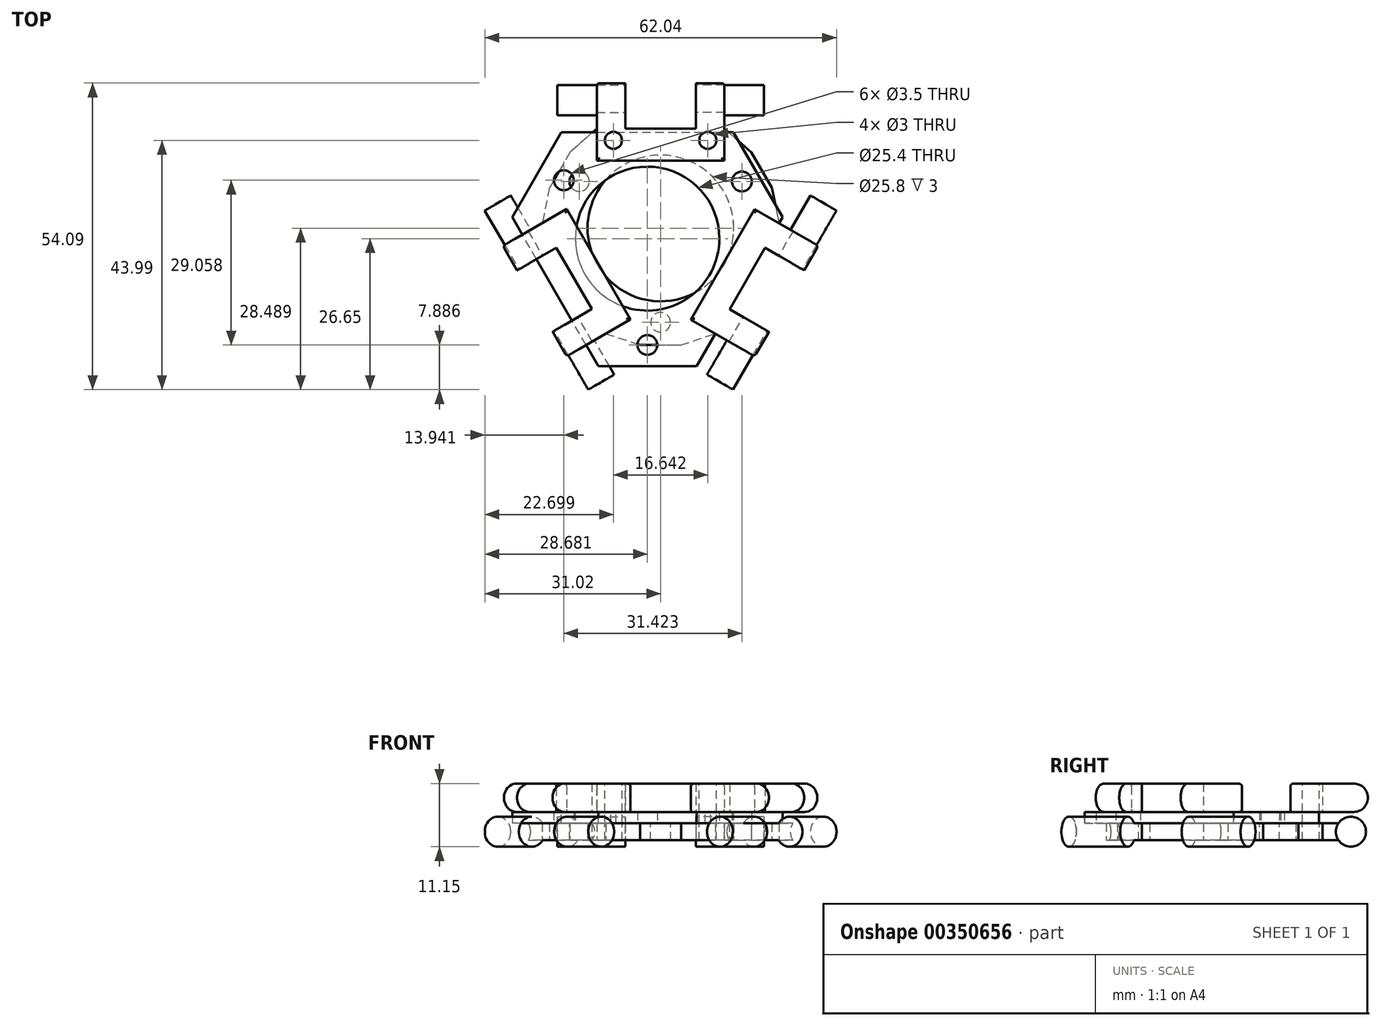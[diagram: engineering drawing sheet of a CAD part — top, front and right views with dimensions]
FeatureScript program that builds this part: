
annotation { "Feature Type Name" : "Feature", "Feature Type Description" : "" }
export const myFeature = defineFeature(function(context is Context, id is Id, definition is map)
    precondition{}
    {
        {
            var Q0;
            Q0=qCreatedBy(makeId("Top.planeOp"),FACE);
            var sketch = newSketch(context, id + "F0", { "sketchPlane" : qUnion([Q0])});
            skLineSegment(sketch, "E0", {"start": v(11.25, 26.96) * mm, "end": v(11.25, 31.96) * mm});
            skLineSegment(sketch, "E1", {"start": v(11.25, 31.96) * mm, "end": v(6.25, 31.96) * mm});
            skLineSegment(sketch, "E2", {"start": v(6.25, 31.96) * mm, "end": v(6.25, 26.96) * mm});
            skLineSegment(sketch, "E3", {"start": v(6.25, 26.96) * mm, "end": v(-6.25, 26.96) * mm});
            skLineSegment(sketch, "E4", {"start": v(-6.25, 26.96) * mm, "end": v(-6.25, 31.96) * mm});
            skLineSegment(sketch, "E5", {"start": v(-6.25, 31.96) * mm, "end": v(-11.25, 31.96) * mm});
            skLineSegment(sketch, "E6", {"start": v(-11.25, 31.96) * mm, "end": v(-11.25, 26.96) * mm});
            skLineSegment(sketch, "E7", {"start": v(11.25, 26.96) * mm, "end": v(16, 22.72) * mm});
            skLineSegment(sketch, "E8", {"start": v(-11.25, 26.96) * mm, "end": v(-16, 22.72) * mm});
            skLineSegment(sketch, "E9", {"start": v(16, 22.72) * mm, "end": v(19.6, 16.48) * mm});
            skLineSegment(sketch, "E10", {"start": v(-16, 22.72) * mm, "end": v(-19.6, 16.48) * mm});
            skLineSegment(sketch, "E11", {"start": v(-19.6, 16.48) * mm, "end": v(-20.9, 10.24) * mm});
            skLineSegment(sketch, "E12", {"start": v(19.6, 16.48) * mm, "end": v(20.9, 10.24) * mm});
            skLineSegment(sketch, "E13", {"start": v(-20.9, 10.24) * mm, "end": v(-25.23, 7.74) * mm});
            skLineSegment(sketch, "E14", {"start": v(-25.23, 7.74) * mm, "end": v(-22.73, 3.41) * mm});
            skLineSegment(sketch, "E15", {"start": v(-22.73, 3.41) * mm, "end": v(-18.4, 5.91) * mm});
            skLineSegment(sketch, "E16", {"start": v(-18.4, 5.91) * mm, "end": v(-12.15, -4.91) * mm});
            skLineSegment(sketch, "E17", {"start": v(-12.15, -4.91) * mm, "end": v(-16.48, -7.41) * mm});
            skLineSegment(sketch, "E18", {"start": v(-16.48, -7.41) * mm, "end": v(-13.98, -11.74) * mm});
            skLineSegment(sketch, "E19", {"start": v(-13.98, -11.74) * mm, "end": v(-9.65, -9.24) * mm});
            skLineSegment(sketch, "E20", {"start": v(20.9, 10.24) * mm, "end": v(25.23, 7.74) * mm});
            skLineSegment(sketch, "E21", {"start": v(25.23, 7.74) * mm, "end": v(22.73, 3.41) * mm});
            skLineSegment(sketch, "E22", {"start": v(22.73, 3.41) * mm, "end": v(18.4, 5.91) * mm});
            skLineSegment(sketch, "E23", {"start": v(18.4, 5.91) * mm, "end": v(12.15, -4.91) * mm});
            skLineSegment(sketch, "E24", {"start": v(12.15, -4.91) * mm, "end": v(16.48, -7.41) * mm});
            skLineSegment(sketch, "E25", {"start": v(16.48, -7.41) * mm, "end": v(13.98, -11.74) * mm});
            skLineSegment(sketch, "E26", {"start": v(13.98, -11.74) * mm, "end": v(9.65, -9.24) * mm});
            skLineSegment(sketch, "E27", {"start": v(-9.65, -9.24) * mm, "end": v(-3.6, -11.24) * mm});
            skLineSegment(sketch, "E28", {"start": v(-3.6, -11.24) * mm, "end": v(3.6, -11.24) * mm});
            skLineSegment(sketch, "E29", {"start": v(3.6, -11.24) * mm, "end": v(9.65, -9.24) * mm});
            skPoint(sketch, "E30.first.point", {"position": v(0, 26.96) * mm});
            skPoint(sketch, "E30.second.point", {"position": v(15.27, 0.5) * mm});
            skPoint(sketch, "E30.third.point", {"position": v(-15.27, 0.5) * mm});
            skCircle(sketch, "E31", {"center": v(0, 9.36) * mm, "radius": 12.9 * mm});
            skLineSegment(sketch, "E32", {"start": v(-17.8, 19.6) * mm, "end": v(15.27, 0.5) * mm, "construction": true});
            skLineSegment(sketch, "E33", {"start": v(17.8, 19.6) * mm, "end": v(-15.27, 0.5) * mm, "construction": true});
            skLineSegment(sketch, "E34", {"start": v(0, -11.24) * mm, "end": v(0, 26.96) * mm, "construction": true});
            skSolve(sketch);
        }
        {
            var Q0;
            Q0=qSketchRegion(id+"F0",true);
            extrude(context, id + "F1", {"entities" : qUnion([Q0]), "depth" : 3 * mm});
        }
        {
            var Q0;
            Q0=makeQuery(id+"F1.opExtrude","CAP_FACE",FACE,{"disambiguationData":[OSD([sQuery(id+"F0.wireOp",EDGE,"E0"),sQuery(id+"F0.wireOp",EDGE,"E1"),sQuery(id+"F0.wireOp",EDGE,"E2"),sQuery(id+"F0.wireOp",EDGE,"E3"),sQuery(id+"F0.wireOp",EDGE,"E4"),sQuery(id+"F0.wireOp",EDGE,"E5"),sQuery(id+"F0.wireOp",EDGE,"E6"),sQuery(id+"F0.wireOp",EDGE,"E7"),sQuery(id+"F0.wireOp",EDGE,"E8"),sQuery(id+"F0.wireOp",EDGE,"E9"),sQuery(id+"F0.wireOp",EDGE,"E10"),sQuery(id+"F0.wireOp",EDGE,"E11"),sQuery(id+"F0.wireOp",EDGE,"E12"),sQuery(id+"F0.wireOp",EDGE,"E13"),sQuery(id+"F0.wireOp",EDGE,"E14"),sQuery(id+"F0.wireOp",EDGE,"E15"),sQuery(id+"F0.wireOp",EDGE,"E16"),sQuery(id+"F0.wireOp",EDGE,"E17"),sQuery(id+"F0.wireOp",EDGE,"E18"),sQuery(id+"F0.wireOp",EDGE,"E19"),sQuery(id+"F0.wireOp",EDGE,"E20"),sQuery(id+"F0.wireOp",EDGE,"E21"),sQuery(id+"F0.wireOp",EDGE,"E22"),sQuery(id+"F0.wireOp",EDGE,"E23"),sQuery(id+"F0.wireOp",EDGE,"E24"),sQuery(id+"F0.wireOp",EDGE,"E25"),sQuery(id+"F0.wireOp",EDGE,"E26"),sQuery(id+"F0.wireOp",EDGE,"E27"),sQuery(id+"F0.wireOp",EDGE,"E28"),sQuery(id+"F0.wireOp",EDGE,"E29"),sQuery(id+"F0.wireOp",EDGE,"E31")])],"isStart":false});
            var sketch = newSketch(context, id + "F2", { "sketchPlane" : qUnion([Q0])});
            skCircle(sketch, "E35", {"center": v(-14.34, 17.6) * mm, "radius": 1.75 * mm});
            skCircle(sketch, "E36", {"center": v(14.34, 17.6) * mm, "radius": 1.75 * mm});
            skCircle(sketch, "E37", {"center": v(0, -7.24) * mm, "radius": 1.75 * mm});
            skLineSegment(sketch, "E38", {"start": v(0, -7.24) * mm, "end": v(3.6, -11.24) * mm, "construction": true});
            skLineSegment(sketch, "E39", {"start": v(0, -7.24) * mm, "end": v(-3.6, -11.24) * mm, "construction": true});
            skLineSegment(sketch, "E40", {"start": v(16, 22.72) * mm, "end": v(14.34, 17.6) * mm, "construction": true});
            skLineSegment(sketch, "E41", {"start": v(19.6, 16.48) * mm, "end": v(14.34, 17.6) * mm, "construction": true});
            skLineSegment(sketch, "E42", {"start": v(-16, 22.72) * mm, "end": v(-14.34, 17.6) * mm, "construction": true});
            skLineSegment(sketch, "E43", {"start": v(-19.6, 16.48) * mm, "end": v(-14.34, 17.6) * mm, "construction": true});
            skLineSegment(sketch, "E44", {"start": v(-14.34, 17.6) * mm, "end": v(14.34, 17.6) * mm, "construction": true});
            skLineSegment(sketch, "E45", {"start": v(14.34, 17.6) * mm, "end": v(0, -7.24) * mm, "construction": true});
            skLineSegment(sketch, "E46", {"start": v(0, -7.24) * mm, "end": v(-14.34, 17.6) * mm, "construction": true});
            skSolve(sketch);
        }
        {
            var Q0;
            Q0=qSketchRegion(id+"F2",true);
            extrude(context, id + "F3", {"entities" : qUnion([Q0]), "operationType" : NewBodyOperationType.REMOVE, "endBound" : BoundingType.THROUGH_ALL, "oppositeDirection" : true, "depth" : 25 * mm});
        }
        {
            var Q0;
            Q0=makeQuery(id+"F1.opExtrude","SWEPT_FACE",FACE,{"disambiguationData":[OSD([sQuery(id+"F0.wireOp",EDGE,"E2")])]});
            var sketch = newSketch(context, id + "F4", { "sketchPlane" : qUnion([Q0])});
            skCircle(sketch, "E47", {"center": v(-31.96, 1.5) * mm, "radius": 2.65 * mm});
            skSolve(sketch);
        }
        {
            var Q0;
            Q0=qSketchRegion(id+"F4",true);
            var Q1;
            Q1=makeQuery(id+"F1.opExtrude","SWEPT_FACE",FACE,{"disambiguationData":[OSD([sQuery(id+"F0.wireOp",EDGE,"E0")])]});
            extrude(context, id + "F5", {"entities" : qUnion([Q0]), "operationType" : NewBodyOperationType.ADD, "oppositeDirection" : true, "endBoundEntityFace" : qUnion([Q1]), "depth" : 12 * mm});
        }
        {
            var Q0;
            Q0=makeQuery(id+"F1.opExtrude","SWEPT_FACE",FACE,{"disambiguationData":[OSD([sQuery(id+"F0.wireOp",EDGE,"E4")])]});
            var sketch = newSketch(context, id + "F6", { "sketchPlane" : qUnion([Q0])});
            skCircle(sketch, "E48", {"center": v(31.96, 1.5) * mm, "radius": 2.65 * mm});
            skSolve(sketch);
        }
        {
            var Q0;
            Q0=qSketchRegion(id+"F6",true);
            extrude(context, id + "F7", {"entities" : qUnion([Q0]), "operationType" : NewBodyOperationType.ADD, "oppositeDirection" : true, "depth" : 12 * mm});
        }
        {
            var Q0;
            Q0=makeQuery(id+"F1.opExtrude","SWEPT_FACE",FACE,{"disambiguationData":[OSD([sQuery(id+"F0.wireOp",EDGE,"E15")])]});
            var sketch = newSketch(context, id + "F8", { "sketchPlane" : qUnion([Q0])});
            skCircle(sketch, "E49", {"center": v(-17.98, 1.5) * mm, "radius": 2.65 * mm});
            skSolve(sketch);
        }
        {
            var Q0;
            Q0=qSketchRegion(id+"F8",true);
            extrude(context, id + "F9", {"entities" : qUnion([Q0]), "operationType" : NewBodyOperationType.ADD, "oppositeDirection" : true, "depth" : 12 * mm});
        }
        {
            var Q0;
            Q0=makeQuery(id+"F1.opExtrude","SWEPT_FACE",FACE,{"disambiguationData":[OSD([sQuery(id+"F0.wireOp",EDGE,"E17")])]});
            var sketch = newSketch(context, id + "F10", { "sketchPlane" : qUnion([Q0])});
            skCircle(sketch, "E50", {"center": v(17.98, 1.5) * mm, "radius": 2.65 * mm});
            skSolve(sketch);
        }
        {
            var Q0;
            Q0=qSketchRegion(id+"F10",true);
            extrude(context, id + "F11", {"entities" : qUnion([Q0]), "operationType" : NewBodyOperationType.ADD, "oppositeDirection" : true, "depth" : 12 * mm});
        }
        {
            var Q0;
            Q0=makeQuery(id+"F1.opExtrude","SWEPT_FACE",FACE,{"disambiguationData":[OSD([sQuery(id+"F0.wireOp",EDGE,"E24")])]});
            var sketch = newSketch(context, id + "F12", { "sketchPlane" : qUnion([Q0])});
            skCircle(sketch, "E51", {"center": v(-17.98, 1.5) * mm, "radius": 2.65 * mm});
            skSolve(sketch);
        }
        {
            var Q0;
            Q0=qSketchRegion(id+"F12",true);
            extrude(context, id + "F13", {"entities" : qUnion([Q0]), "operationType" : NewBodyOperationType.ADD, "oppositeDirection" : true, "depth" : 12 * mm});
        }
        {
            var Q0;
            Q0=makeQuery(id+"F1.opExtrude","SWEPT_FACE",FACE,{"disambiguationData":[OSD([sQuery(id+"F0.wireOp",EDGE,"E22")])]});
            var sketch = newSketch(context, id + "F14", { "sketchPlane" : qUnion([Q0])});
            skCircle(sketch, "E52", {"center": v(17.98, 1.5) * mm, "radius": 2.65 * mm});
            skSolve(sketch);
        }
        {
            var Q0;
            Q0=qSketchRegion(id+"F14",true);
            extrude(context, id + "F15", {"entities" : qUnion([Q0]), "operationType" : NewBodyOperationType.ADD, "oppositeDirection" : true, "depth" : 12 * mm});
        }
        {
            var Q0;
            Q0=makeQuery(id+"F1.opExtrude","CAP_FACE",FACE,{"disambiguationData":[OSD([sQuery(id+"F0.wireOp",EDGE,"E0"),sQuery(id+"F0.wireOp",EDGE,"E1"),sQuery(id+"F0.wireOp",EDGE,"E2"),sQuery(id+"F0.wireOp",EDGE,"E3"),sQuery(id+"F0.wireOp",EDGE,"E4"),sQuery(id+"F0.wireOp",EDGE,"E5"),sQuery(id+"F0.wireOp",EDGE,"E6"),sQuery(id+"F0.wireOp",EDGE,"E7"),sQuery(id+"F0.wireOp",EDGE,"E8"),sQuery(id+"F0.wireOp",EDGE,"E9"),sQuery(id+"F0.wireOp",EDGE,"E10"),sQuery(id+"F0.wireOp",EDGE,"E11"),sQuery(id+"F0.wireOp",EDGE,"E12"),sQuery(id+"F0.wireOp",EDGE,"E13"),sQuery(id+"F0.wireOp",EDGE,"E14"),sQuery(id+"F0.wireOp",EDGE,"E15"),sQuery(id+"F0.wireOp",EDGE,"E16"),sQuery(id+"F0.wireOp",EDGE,"E17"),sQuery(id+"F0.wireOp",EDGE,"E18"),sQuery(id+"F0.wireOp",EDGE,"E19"),sQuery(id+"F0.wireOp",EDGE,"E20"),sQuery(id+"F0.wireOp",EDGE,"E21"),sQuery(id+"F0.wireOp",EDGE,"E22"),sQuery(id+"F0.wireOp",EDGE,"E23"),sQuery(id+"F0.wireOp",EDGE,"E24"),sQuery(id+"F0.wireOp",EDGE,"E25"),sQuery(id+"F0.wireOp",EDGE,"E26"),sQuery(id+"F0.wireOp",EDGE,"E27"),sQuery(id+"F0.wireOp",EDGE,"E28"),sQuery(id+"F0.wireOp",EDGE,"E29"),sQuery(id+"F0.wireOp",EDGE,"E31")])],"isStart":false});
            var sketch = newSketch(context, id + "F16", { "sketchPlane" : qUnion([Q0])});
            skLineSegment(sketch, "E53", {"start": v(-34.84, 26.28) * mm, "end": v(30.16, 26.28) * mm});
            skLineSegment(sketch, "E54", {"start": v(30.16, 26.28) * mm, "end": v(-2.34, -30) * mm});
            skLineSegment(sketch, "E55", {"start": v(-2.34, -30) * mm, "end": v(-34.84, 26.28) * mm});
            skCircle(sketch, "E56", {"center": v(-2.34, 7.52) * mm, "radius": 12.7 * mm});
            skCircle(sketch, "E57", {"center": v(-17.08, 17.81) * mm, "radius": 1.75 * mm});
            skCircle(sketch, "E58", {"center": v(14.34, 17.6) * mm, "radius": 1.75 * mm});
            skCircle(sketch, "E59", {"center": v(-2.34, -11.24) * mm, "radius": 1.75 * mm});
            skLineSegment(sketch, "E60", {"start": v(-2.34, 7.52) * mm, "end": v(30.16, 26.28) * mm, "construction": true});
            skLineSegment(sketch, "E61", {"start": v(-2.34, 7.52) * mm, "end": v(-34.84, 26.28) * mm, "construction": true});
            skLineSegment(sketch, "E62", {"start": v(-2.34, 7.52) * mm, "end": v(-2.34, -30) * mm, "construction": true});
            skSolve(sketch);
        }
        {
            var Q0;
            Q0 = qSketchRegion(id + "F16", true);
            extrude(context, id + "F17", {"entities" : qUnion([Q0]), "depth" : 2 * mm});
        }
        {
            var Q0;
            Q0=makeQuery(id+"F17.opExtrude","SWEPT_EDGE",EDGE,{"disambiguationData":[OSD([sQuery(id+"F16.wireOp",EDGE,"E54"),sQuery(id+"F16.wireOp",EDGE,"E55")])]});
            var Q1;
            Q1=makeQuery(id+"F17.opExtrude","SWEPT_EDGE",EDGE,{"disambiguationData":[OSD([sQuery(id+"F16.wireOp",EDGE,"E53"),sQuery(id+"F16.wireOp",EDGE,"E54")])]});
            var Q2;
            Q2=makeQuery(id+"F17.opExtrude","SWEPT_EDGE",EDGE,{"disambiguationData":[OSD([sQuery(id+"F16.wireOp",EDGE,"E53"),sQuery(id+"F16.wireOp",EDGE,"E55")])]});
            chamfer(context, id + "F18", {"entities" : qUnion([Q0, Q1, Q2]), "width" : 10 * mm, "tangentPropagation" : true});
        }
        {
            var Q0;
            Q0=makeQuery(id+"F17.opExtrude","CAP_FACE",FACE,{"disambiguationData":[OSD([sQuery(id+"F16.wireOp",EDGE,"E53"),sQuery(id+"F16.wireOp",EDGE,"E54"),sQuery(id+"F16.wireOp",EDGE,"E55"),sQuery(id+"F16.wireOp",EDGE,"E56"),sQuery(id+"F16.wireOp",EDGE,"E57"),sQuery(id+"F16.wireOp",EDGE,"E58"),sQuery(id+"F16.wireOp",EDGE,"E59")])],"isStart":false});
            var sketch = newSketch(context, id + "F19", { "sketchPlane" : qUnion([Q0])});
            skLineSegment(sketch, "E63", {"start": v(-18.4, 5.91) * mm, "end": v(-25.33, 1.91) * mm});
            skLineSegment(sketch, "E64", {"start": v(-25.33, 1.91) * mm, "end": v(-27.83, 6.24) * mm});
            skLineSegment(sketch, "E65", {"start": v(-19.08, -8.91) * mm, "end": v(-12.15, -4.91) * mm});
            skLineSegment(sketch, "E66", {"start": v(-16.58, -13.24) * mm, "end": v(-19.08, -8.91) * mm});
            skLineSegment(sketch, "E67", {"start": v(12.16, -4.92) * mm, "end": v(19.1, -8.92) * mm});
            skLineSegment(sketch, "E68", {"start": v(19.1, -8.92) * mm, "end": v(16.6, -13.25) * mm});
            skLineSegment(sketch, "E69", {"start": v(27.83, 6.24) * mm, "end": v(25.33, 1.91) * mm});
            skLineSegment(sketch, "E70", {"start": v(25.33, 1.91) * mm, "end": v(18.4, 5.91) * mm});
            skLineSegment(sketch, "E71", {"start": v(6.25, 34.96) * mm, "end": v(11.25, 34.96) * mm});
            skLineSegment(sketch, "E72", {"start": v(6.25, 26.96) * mm, "end": v(6.25, 34.96) * mm});
            skLineSegment(sketch, "E73", {"start": v(-11.25, 34.96) * mm, "end": v(-6.25, 34.96) * mm});
            skLineSegment(sketch, "E74", {"start": v(-6.25, 34.96) * mm, "end": v(-6.25, 26.96) * mm});
            skLineSegment(sketch, "E75", {"start": v(-18.4, 5.91) * mm, "end": v(-12.15, -4.91) * mm});
            skLineSegment(sketch, "E76", {"start": v(-16.58, -13.24) * mm, "end": v(-5.32, -6.74) * mm});
            skLineSegment(sketch, "E77", {"start": v(-5.32, -6.74) * mm, "end": v(-16.57, 12.74) * mm});
            skLineSegment(sketch, "E78", {"start": v(-16.57, 12.74) * mm, "end": v(-27.83, 6.24) * mm});
            skLineSegment(sketch, "E79", {"start": v(16.6, -13.25) * mm, "end": v(5.34, -6.77) * mm});
            skLineSegment(sketch, "E80", {"start": v(5.34, -6.77) * mm, "end": v(16.56, 12.73) * mm});
            skLineSegment(sketch, "E81", {"start": v(16.56, 12.73) * mm, "end": v(27.83, 6.24) * mm});
            skLineSegment(sketch, "E82", {"start": v(-11.25, 34.96) * mm, "end": v(-11.25, 21.28) * mm});
            skLineSegment(sketch, "E83", {"start": v(-11.25, 21.28) * mm, "end": v(11.25, 21.28) * mm});
            skLineSegment(sketch, "E84", {"start": v(11.25, 21.28) * mm, "end": v(11.25, 34.96) * mm});
            skLineSegment(sketch, "E85", {"start": v(12.16, -4.92) * mm, "end": v(18.4, 5.91) * mm});
            skLineSegment(sketch, "E86", {"start": v(-6.25, 26.96) * mm, "end": v(6.25, 26.96) * mm});
            skSolve(sketch);
        }
        {
            var Q0;
            Q0 = qSketchRegion(id + "F19", true);
            extrude(context, id + "F20", {"entities" : qUnion([Q0]), "depth" : 5 * mm});
        }
        {
            var Q0;
            Q0=makeQuery(id+"F20.opExtrude","CAP_EDGE",EDGE,{"disambiguationData":[OSD([sQuery(id+"F19.wireOp",EDGE,"E66")])],"isStart":false});
            var Q1;
            Q1=makeQuery(id+"F20.opExtrude","CAP_EDGE",EDGE,{"disambiguationData":[OSD([sQuery(id+"F19.wireOp",EDGE,"E66")])],"isStart":true});
            var Q2;
            Q2=makeQuery(id+"F20.opExtrude","CAP_EDGE",EDGE,{"disambiguationData":[OSD([sQuery(id+"F19.wireOp",EDGE,"E64")])],"isStart":false});
            var Q3;
            Q3=makeQuery(id+"F20.opExtrude","CAP_EDGE",EDGE,{"disambiguationData":[OSD([sQuery(id+"F19.wireOp",EDGE,"E64")])],"isStart":true});
            var Q4;
            Q4=makeQuery(id+"F20.opExtrude","CAP_EDGE",EDGE,{"disambiguationData":[OSD([sQuery(id+"F19.wireOp",EDGE,"E68")])],"isStart":false});
            var Q5;
            Q5=makeQuery(id+"F20.opExtrude","CAP_EDGE",EDGE,{"disambiguationData":[OSD([sQuery(id+"F19.wireOp",EDGE,"E68")])],"isStart":true});
            var Q6;
            Q6=makeQuery(id+"F20.opExtrude","CAP_EDGE",EDGE,{"disambiguationData":[OSD([sQuery(id+"F19.wireOp",EDGE,"E69")])],"isStart":false});
            var Q7;
            Q7=makeQuery(id+"F20.opExtrude","CAP_EDGE",EDGE,{"disambiguationData":[OSD([sQuery(id+"F19.wireOp",EDGE,"E69")])],"isStart":true});
            var Q8;
            Q8=makeQuery(id+"F20.opExtrude","CAP_EDGE",EDGE,{"disambiguationData":[OSD([sQuery(id+"F19.wireOp",EDGE,"E73")])],"isStart":false});
            var Q9;
            Q9=makeQuery(id+"F20.opExtrude","CAP_EDGE",EDGE,{"disambiguationData":[OSD([sQuery(id+"F19.wireOp",EDGE,"E73")])],"isStart":true});
            var Q10;
            Q10=makeQuery(id+"F20.opExtrude","CAP_EDGE",EDGE,{"disambiguationData":[OSD([sQuery(id+"F19.wireOp",EDGE,"E71")])],"isStart":true});
            var Q11;
            Q11=makeQuery(id+"F20.opExtrude","CAP_EDGE",EDGE,{"disambiguationData":[OSD([sQuery(id+"F19.wireOp",EDGE,"E71")])],"isStart":false});
            fillet(context, id + "F21", {"entities" : qUnion([Q0, Q1, Q2, Q3, Q4, Q5, Q6, Q7, Q8, Q9, Q10, Q11]), "radius" : 2.5 * mm, "tangentPropagation" : true, "allowEdgeOverflow" : false});
        }
        {
            var Q0;
            Q0=makeQuery(id+"F20.opExtrude","CAP_EDGE",EDGE,{"disambiguationData":[OSD([sQuery(id+"F19.wireOp",EDGE,"E83")])],"isStart":false});
            var Q1;
            Q1=makeQuery(id+"F20.opExtrude","CAP_EDGE",EDGE,{"disambiguationData":[OSD([sQuery(id+"F19.wireOp",EDGE,"E80")])],"isStart":false});
            var Q2;
            Q2=makeQuery(id+"F20.opExtrude","CAP_EDGE",EDGE,{"disambiguationData":[OSD([sQuery(id+"F19.wireOp",EDGE,"E77")])],"isStart":false});
            var Q3;
            Q3=makeQuery(id+"F20.opExtrude","CAP_EDGE",EDGE,{"disambiguationData":[OSD([sQuery(id+"F19.wireOp",EDGE,"E84")])],"isStart":false});
            var Q4;
            Q4=makeQuery(id+"F20.opExtrude","CAP_EDGE",EDGE,{"disambiguationData":[OSD([sQuery(id+"F19.wireOp",EDGE,"E82")])],"isStart":false});
            var Q5;
            Q5=makeQuery(id+"F20.opExtrude","CAP_EDGE",EDGE,{"disambiguationData":[OSD([sQuery(id+"F19.wireOp",EDGE,"E78")])],"isStart":false});
            var Q6;
            Q6=makeQuery(id+"F20.opExtrude","CAP_EDGE",EDGE,{"disambiguationData":[OSD([sQuery(id+"F19.wireOp",EDGE,"E76")])],"isStart":false});
            var Q7;
            Q7=makeQuery(id+"F20.opExtrude","CAP_EDGE",EDGE,{"disambiguationData":[OSD([sQuery(id+"F19.wireOp",EDGE,"E79")])],"isStart":false});
            var Q8;
            Q8=makeQuery(id+"F20.opExtrude","CAP_EDGE",EDGE,{"disambiguationData":[OSD([sQuery(id+"F19.wireOp",EDGE,"E81")])],"isStart":false});
            fillet(context, id + "F22", {"entities" : qUnion([Q0, Q1, Q2, Q3, Q4, Q5, Q6, Q7, Q8]), "radius" : .5 * mm, "tangentPropagation" : true, "allowEdgeOverflow" : false});
        }
        {
            var Q0;
            Q0=makeQuery(id+"F20.opExtrude","CAP_FACE",FACE,{"disambiguationData":[OSD([sQuery(id+"F19.wireOp",EDGE,"E71"),sQuery(id+"F19.wireOp",EDGE,"E72"),sQuery(id+"F19.wireOp",EDGE,"E73"),sQuery(id+"F19.wireOp",EDGE,"E74"),sQuery(id+"F19.wireOp",EDGE,"E82"),sQuery(id+"F19.wireOp",EDGE,"E83"),sQuery(id+"F19.wireOp",EDGE,"E84"),sQuery(id+"F19.wireOp",EDGE,"E86")])],"isStart":false});
            var sketch = newSketch(context, id + "F23", { "sketchPlane" : qUnion([Q0])});
            skCircle(sketch, "E87", {"center": v(-8.32, 24.86) * mm, "radius": 1.5 * mm});
            skCircle(sketch, "E88", {"center": v(8.32, 24.86) * mm, "radius": 1.5 * mm});
            skLineSegment(sketch, "E89", {"start": v(-8.32, 24.86) * mm, "end": v(8.32, 24.86) * mm, "construction": true});
            skSolve(sketch);
        }
        {
            var Q0;
            Q0 = qSketchRegion(id + "F23", true);
            extrude(context, id + "F24", {"entities" : qUnion([Q0]), "operationType" : NewBodyOperationType.REMOVE, "endBound" : BoundingType.THROUGH_ALL, "oppositeDirection" : true, "depth" : 25 * mm});
        }
    });
